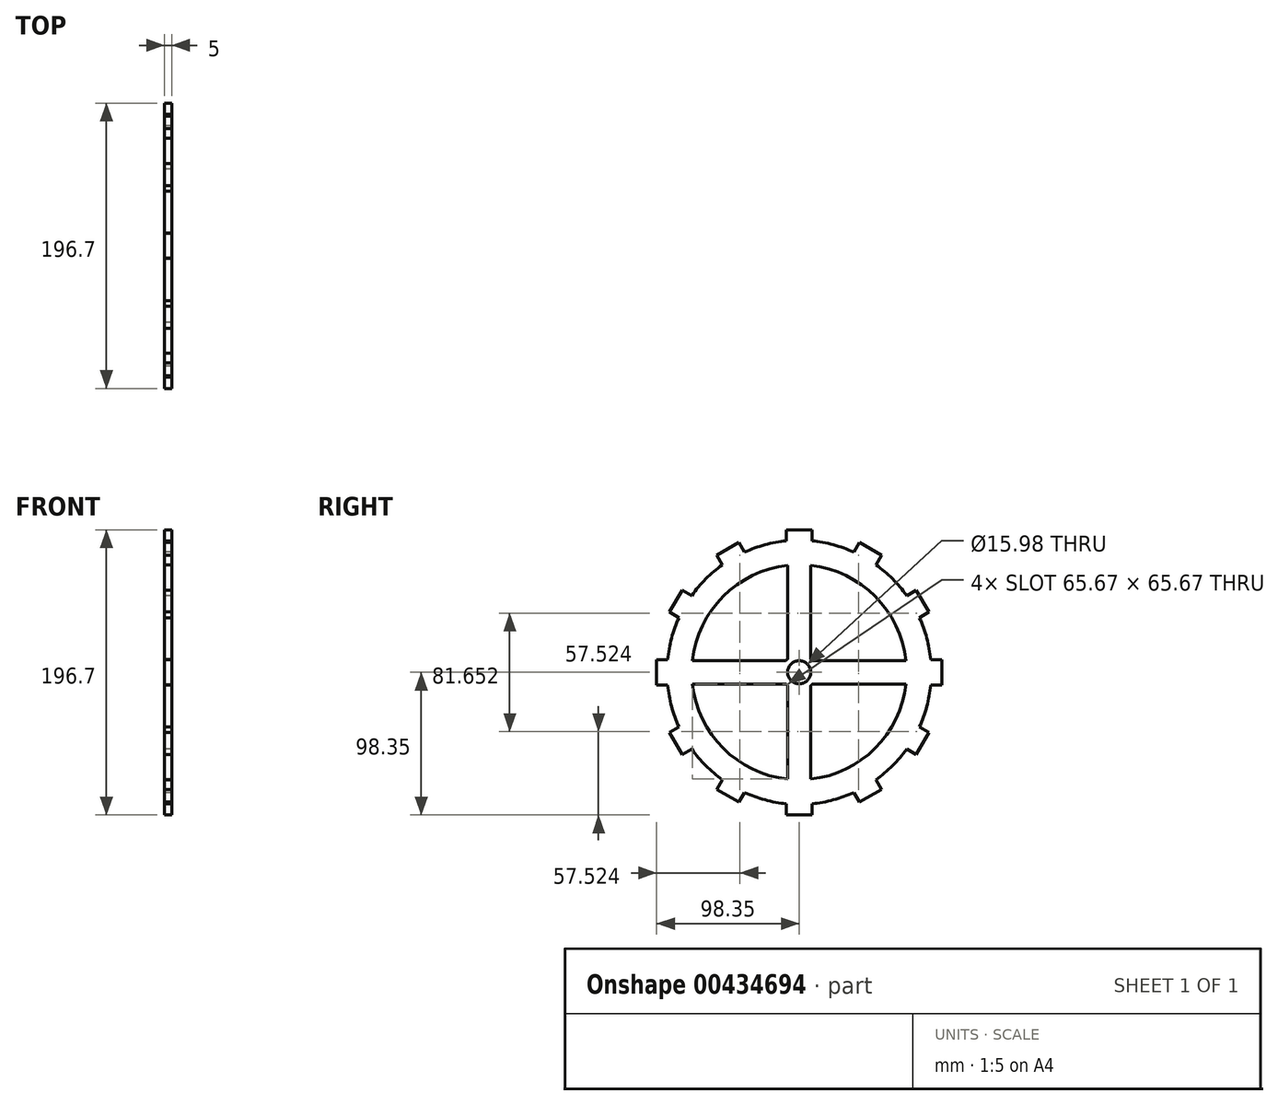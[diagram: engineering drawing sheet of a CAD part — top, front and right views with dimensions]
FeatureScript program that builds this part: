
annotation { "Feature Type Name" : "Feature", "Feature Type Description" : "" }
export const myFeature = defineFeature(function(context is Context, id is Id, definition is map)
    precondition{}
    {
        {
            var Q0;
            Q0=qCreatedBy(makeId("Right.planeOp"),FACE);
            var sketch = newSketch(context, id + "F0", { "sketchPlane" : qUnion([Q0])});
            skLineSegment(sketch, "E0", {"start": v(-91.09, 0) * mm, "end": v(91.09, 0) * mm, "construction": true});
            skLineSegment(sketch, "E1", {"start": v(0, 91.09) * mm, "end": v(0, -91.09) * mm, "construction": true});
            skCircle(sketch, "E2", {"center": v(0, 0) * mm, "radius": 8 * mm});
            skCircle(sketch, "E3", {"center": v(0, 0) * mm, "radius": 12.19 * mm});
            skCircle(sketch, "E4", {"center": v(0, 0) * mm, "radius": 74.1 * mm});
            skCircle(sketch, "E5", {"center": v(0, 0) * mm, "radius": 91.09 * mm});
            skLineSegment(sketch, "E6", {"start": v(0, 12.19) * mm, "end": v(30.8, 12.19) * mm, "construction": true});
            skLineSegment(sketch, "E7", {"start": v(0, -12.19) * mm, "end": v(30.8, -12.19) * mm, "construction": true});
            skLineSegment(sketch, "E8", {"start": v(-12.19, 0) * mm, "end": v(-12.19, 23.25) * mm, "construction": true});
            skLineSegment(sketch, "E9", {"start": v(12.19, 0) * mm, "end": v(12.19, 23.25) * mm, "construction": true});
            skLineSegment(sketch, "E10", {"start": v(-8, 0) * mm, "end": v(-8, 23.25) * mm, "construction": true});
            skLineSegment(sketch, "E11", {"start": v(8, 0) * mm, "end": v(8, 23.25) * mm, "construction": true});
            skLineSegment(sketch, "E12", {"start": v(0, 8) * mm, "end": v(30.42, 8) * mm, "construction": true});
            skLineSegment(sketch, "E13", {"start": v(0, -8) * mm, "end": v(30.42, -8) * mm, "construction": true});
            skLineSegment(sketch, "E14", {"start": v(-8, 9.2) * mm, "end": v(-30.06, 9.2) * mm, "construction": true});
            skLineSegment(sketch, "E15", {"start": v(-8, -9.2) * mm, "end": v(-30.06, -9.2) * mm, "construction": true});
            skLineSegment(sketch, "E16", {"start": v(-8, 9.2) * mm, "end": v(-8, 73.66) * mm});
            skLineSegment(sketch, "E17", {"start": v(9.2, 8) * mm, "end": v(9.2, 27.63) * mm, "construction": true});
            skLineSegment(sketch, "E18", {"start": v(9.2, 8) * mm, "end": v(73.66, 8) * mm});
            skLineSegment(sketch, "E19.MirrorCS", {"start": v(8, 9.2) * mm, "end": v(8, 73.66) * mm});
            skLineSegment(sketch, "E20.MirrorCS", {"start": v(-9.2, 8) * mm, "end": v(-73.66, 8) * mm});
            skLineSegment(sketch, "E21.MirrorCS", {"start": v(-8, -9.2) * mm, "end": v(-8, -73.66) * mm});
            skLineSegment(sketch, "E22.MirrorCS", {"start": v(8, -9.2) * mm, "end": v(8, -73.66) * mm});
            skLineSegment(sketch, "E23.MirrorCS", {"start": v(-9.2, -8) * mm, "end": v(-73.66, -8) * mm});
            skLineSegment(sketch, "E24.MirrorCS", {"start": v(9.2, -8) * mm, "end": v(73.66, -8) * mm});
            skLineSegment(sketch, "E25", {"start": v(-8.78, 90.66) * mm, "end": v(-8.78, 98.35) * mm});
            skLineSegment(sketch, "E26", {"start": v(-8.78, 98.35) * mm, "end": v(0, 98.35) * mm});
            skLineSegment(sketch, "E27.MirrorCS", {"start": v(8.78, 90.66) * mm, "end": v(8.78, 98.35) * mm});
            skLineSegment(sketch, "E28.MirrorCS", {"start": v(8.78, 98.35) * mm, "end": v(0, 98.35) * mm});
            skLineSegment(sketch, "E29.1.1", {"start": v(-52.93, 74.13) * mm, "end": v(-56.78, 80.79) * mm});
            skLineSegment(sketch, "E29.1.2", {"start": v(-56.78, 80.79) * mm, "end": v(-49.18, 85.18) * mm});
            skLineSegment(sketch, "E29.1.3", {"start": v(-41.58, 89.57) * mm, "end": v(-49.18, 85.18) * mm});
            skLineSegment(sketch, "E29.1.4", {"start": v(-37.73, 82.9) * mm, "end": v(-41.58, 89.57) * mm});
            skLineSegment(sketch, "E29.2.1", {"start": v(-82.9, 37.73) * mm, "end": v(-89.57, 41.58) * mm});
            skLineSegment(sketch, "E29.2.2", {"start": v(-89.57, 41.58) * mm, "end": v(-85.18, 49.18) * mm});
            skLineSegment(sketch, "E29.2.3", {"start": v(-80.79, 56.78) * mm, "end": v(-85.18, 49.18) * mm});
            skLineSegment(sketch, "E29.2.4", {"start": v(-74.13, 52.93) * mm, "end": v(-80.79, 56.78) * mm});
            skLineSegment(sketch, "E29.3.1", {"start": v(-90.66, -8.78) * mm, "end": v(-98.35, -8.78) * mm});
            skLineSegment(sketch, "E29.3.2", {"start": v(-98.35, -8.78) * mm, "end": v(-98.35, 0) * mm});
            skLineSegment(sketch, "E29.3.3", {"start": v(-98.35, 8.78) * mm, "end": v(-98.35, 0) * mm});
            skLineSegment(sketch, "E29.3.4", {"start": v(-90.66, 8.78) * mm, "end": v(-98.35, 8.78) * mm});
            skLineSegment(sketch, "E29.4.1", {"start": v(-74.13, -52.93) * mm, "end": v(-80.79, -56.78) * mm});
            skLineSegment(sketch, "E29.4.2", {"start": v(-80.79, -56.78) * mm, "end": v(-85.18, -49.18) * mm});
            skLineSegment(sketch, "E29.4.3", {"start": v(-89.57, -41.58) * mm, "end": v(-85.18, -49.18) * mm});
            skLineSegment(sketch, "E29.4.4", {"start": v(-82.9, -37.73) * mm, "end": v(-89.57, -41.58) * mm});
            skLineSegment(sketch, "E29.5.1", {"start": v(-37.73, -82.9) * mm, "end": v(-41.58, -89.57) * mm});
            skLineSegment(sketch, "E29.5.2", {"start": v(-41.58, -89.57) * mm, "end": v(-49.18, -85.18) * mm});
            skLineSegment(sketch, "E29.5.3", {"start": v(-56.78, -80.79) * mm, "end": v(-49.18, -85.18) * mm});
            skLineSegment(sketch, "E29.5.4", {"start": v(-52.93, -74.13) * mm, "end": v(-56.78, -80.79) * mm});
            skLineSegment(sketch, "E29.6.1", {"start": v(8.78, -90.66) * mm, "end": v(8.78, -98.35) * mm});
            skLineSegment(sketch, "E29.6.2", {"start": v(8.78, -98.35) * mm, "end": v(0, -98.35) * mm});
            skLineSegment(sketch, "E29.6.3", {"start": v(-8.78, -98.35) * mm, "end": v(0, -98.35) * mm});
            skLineSegment(sketch, "E29.6.4", {"start": v(-8.78, -90.66) * mm, "end": v(-8.78, -98.35) * mm});
            skLineSegment(sketch, "E29.7.1", {"start": v(52.93, -74.13) * mm, "end": v(56.78, -80.79) * mm});
            skLineSegment(sketch, "E29.7.2", {"start": v(56.78, -80.79) * mm, "end": v(49.18, -85.18) * mm});
            skLineSegment(sketch, "E29.7.3", {"start": v(41.58, -89.57) * mm, "end": v(49.18, -85.18) * mm});
            skLineSegment(sketch, "E29.7.4", {"start": v(37.73, -82.9) * mm, "end": v(41.58, -89.57) * mm});
            skLineSegment(sketch, "E29.8.1", {"start": v(82.9, -37.73) * mm, "end": v(89.57, -41.58) * mm});
            skLineSegment(sketch, "E29.8.2", {"start": v(89.57, -41.58) * mm, "end": v(85.18, -49.18) * mm});
            skLineSegment(sketch, "E29.8.3", {"start": v(80.79, -56.78) * mm, "end": v(85.18, -49.18) * mm});
            skLineSegment(sketch, "E29.8.4", {"start": v(74.13, -52.93) * mm, "end": v(80.79, -56.78) * mm});
            skLineSegment(sketch, "E29.9.1", {"start": v(90.66, 8.78) * mm, "end": v(98.35, 8.78) * mm});
            skLineSegment(sketch, "E29.9.2", {"start": v(98.35, 8.78) * mm, "end": v(98.35, 0) * mm});
            skLineSegment(sketch, "E29.9.3", {"start": v(98.35, -8.78) * mm, "end": v(98.35, 0) * mm});
            skLineSegment(sketch, "E29.9.4", {"start": v(90.66, -8.78) * mm, "end": v(98.35, -8.78) * mm});
            skLineSegment(sketch, "E29.10.1", {"start": v(74.13, 52.93) * mm, "end": v(80.79, 56.78) * mm});
            skLineSegment(sketch, "E29.10.2", {"start": v(80.79, 56.78) * mm, "end": v(85.18, 49.18) * mm});
            skLineSegment(sketch, "E29.10.3", {"start": v(89.57, 41.58) * mm, "end": v(85.18, 49.18) * mm});
            skLineSegment(sketch, "E29.10.4", {"start": v(82.9, 37.73) * mm, "end": v(89.57, 41.58) * mm});
            skLineSegment(sketch, "E29.11.1", {"start": v(37.73, 82.9) * mm, "end": v(41.58, 89.57) * mm});
            skLineSegment(sketch, "E29.11.2", {"start": v(41.58, 89.57) * mm, "end": v(49.18, 85.18) * mm});
            skLineSegment(sketch, "E29.11.3", {"start": v(56.78, 80.79) * mm, "end": v(49.18, 85.18) * mm});
            skLineSegment(sketch, "E29.11.4", {"start": v(52.93, 74.13) * mm, "end": v(56.78, 80.79) * mm});
            skSolve(sketch);
        }
        {
            var Q0;
            Q0=makeQuery(id+"F0.imprint","IMPRINT",FACE,{"disambiguationData":[TD([[makeQuery(id+"F0.imprint","IMPRINT",EDGE,{"derivedFrom":sQuery(id+"F0.wireOp",EDGE,"E5")}),1.0]])]});
            var Q1;
            {var subQ0=sQuery(id+"F0.wireOp",EDGE,"E16");Q1=makeQuery(id+"F0.imprint","IMPRINT",FACE,{"disambiguationData":[TD([[makeQuery(id+"F0.imprint","IMPRINT",EDGE,{"derivedFrom":subQ0}),-1.0]])]});}
            var Q2;
            Q2=makeQuery(id+"F0.imprint","IMPRINT",FACE,{"disambiguationData":[TD([[makeQuery(id+"F0.imprint","IMPRINT",EDGE,{"derivedFrom":sQuery(id+"F0.wireOp",EDGE,"E2")}),-1.0]])]});
            var Q3;
            {var subQ0=sQuery(id+"F0.wireOp",EDGE,"E20.MirrorCS");Q3=makeQuery(id+"F0.imprint","IMPRINT",FACE,{"disambiguationData":[TD([[makeQuery(id+"F0.imprint","IMPRINT",EDGE,{"derivedFrom":subQ0}),1.0]])]});}
            var Q4;
            {var subQ0=sQuery(id+"F0.wireOp",EDGE,"E18");Q4=makeQuery(id+"F0.imprint","IMPRINT",FACE,{"disambiguationData":[TD([[makeQuery(id+"F0.imprint","IMPRINT",EDGE,{"derivedFrom":subQ0}),-1.0]])]});}
            var Q5;
            {var subQ0=sQuery(id+"F0.wireOp",EDGE,"E21.MirrorCS");Q5=makeQuery(id+"F0.imprint","IMPRINT",FACE,{"disambiguationData":[TD([[makeQuery(id+"F0.imprint","IMPRINT",EDGE,{"derivedFrom":subQ0}),1.0]])]});}
            var Q6;
            {var subQ11=sQuery(id+"F0.wireOp",EDGE,"E4");var subQ18=makeQuery(id+"F0.imprint","INTERSECT",VERTEX,{"derivedFrom":[subQ11,sQuery(id+"F0.wireOp",EDGE,"E18")]});Q6=makeQuery(id+"F0.imprint","IMPRINT",FACE,{"disambiguationData":[TD([[makeQuery(id+"F0.imprint","IMPRINT",EDGE,{"disambiguationData":[TD([[subQ18,-1.0]])],"derivedFrom":subQ11}),-1.0]])]});}
            var Q7;
            {var subQ1=sQuery(id+"F0.wireOp",EDGE,"E25");Q7=makeQuery(id+"F0.imprint","IMPRINT",FACE,{"disambiguationData":[TD([[makeQuery(id+"F0.imprint","IMPRINT",EDGE,{"derivedFrom":subQ1}),-1.0]])]});}
            var Q8;
            {var subQ0=sQuery(id+"F0.wireOp",EDGE,"E29.11.1");Q8=makeQuery(id+"F0.imprint","IMPRINT",FACE,{"disambiguationData":[TD([[makeQuery(id+"F0.imprint","IMPRINT",EDGE,{"derivedFrom":subQ0}),-1.0]])]});}
            var Q9;
            {var subQ1=sQuery(id+"F0.wireOp",EDGE,"E29.10.1");Q9=makeQuery(id+"F0.imprint","IMPRINT",FACE,{"disambiguationData":[TD([[makeQuery(id+"F0.imprint","IMPRINT",EDGE,{"derivedFrom":subQ1}),-1.0]])]});}
            var Q10;
            {var subQ1=sQuery(id+"F0.wireOp",EDGE,"E29.9.1");Q10=makeQuery(id+"F0.imprint","IMPRINT",FACE,{"disambiguationData":[TD([[makeQuery(id+"F0.imprint","IMPRINT",EDGE,{"derivedFrom":subQ1}),-1.0]])]});}
            var Q11;
            {var subQ2=sQuery(id+"F0.wireOp",EDGE,"E29.8.1");Q11=makeQuery(id+"F0.imprint","IMPRINT",FACE,{"disambiguationData":[TD([[makeQuery(id+"F0.imprint","IMPRINT",EDGE,{"derivedFrom":subQ2}),-1.0]])]});}
            var Q12;
            {var subQ1=sQuery(id+"F0.wireOp",EDGE,"E29.7.1");Q12=makeQuery(id+"F0.imprint","IMPRINT",FACE,{"disambiguationData":[TD([[makeQuery(id+"F0.imprint","IMPRINT",EDGE,{"derivedFrom":subQ1}),-1.0]])]});}
            var Q13;
            {var subQ1=sQuery(id+"F0.wireOp",EDGE,"E29.6.1");Q13=makeQuery(id+"F0.imprint","IMPRINT",FACE,{"disambiguationData":[TD([[makeQuery(id+"F0.imprint","IMPRINT",EDGE,{"derivedFrom":subQ1}),-1.0]])]});}
            var Q14;
            {var subQ1=sQuery(id+"F0.wireOp",EDGE,"E29.5.1");Q14=makeQuery(id+"F0.imprint","IMPRINT",FACE,{"disambiguationData":[TD([[makeQuery(id+"F0.imprint","IMPRINT",EDGE,{"derivedFrom":subQ1}),-1.0]])]});}
            var Q15;
            {var subQ1=sQuery(id+"F0.wireOp",EDGE,"E29.4.1");Q15=makeQuery(id+"F0.imprint","IMPRINT",FACE,{"disambiguationData":[TD([[makeQuery(id+"F0.imprint","IMPRINT",EDGE,{"derivedFrom":subQ1}),-1.0]])]});}
            var Q16;
            {var subQ2=sQuery(id+"F0.wireOp",EDGE,"E29.3.1");Q16=makeQuery(id+"F0.imprint","IMPRINT",FACE,{"disambiguationData":[TD([[makeQuery(id+"F0.imprint","IMPRINT",EDGE,{"derivedFrom":subQ2}),-1.0]])]});}
            var Q17;
            {var subQ2=sQuery(id+"F0.wireOp",EDGE,"E29.2.1");Q17=makeQuery(id+"F0.imprint","IMPRINT",FACE,{"disambiguationData":[TD([[makeQuery(id+"F0.imprint","IMPRINT",EDGE,{"derivedFrom":subQ2}),-1.0]])]});}
            var Q18;
            {var subQ1=sQuery(id+"F0.wireOp",EDGE,"E29.1.1");Q18=makeQuery(id+"F0.imprint","IMPRINT",FACE,{"disambiguationData":[TD([[makeQuery(id+"F0.imprint","IMPRINT",EDGE,{"derivedFrom":subQ1}),-1.0]])]});}
            extrude(context, id + "F1", {"entities" : qUnion([Q0, Q1, Q2, Q3, Q4, Q5, Q6, Q7, Q8, Q9, Q10, Q11, Q12, Q13, Q14, Q15, Q16, Q17, Q18]), "depth" : 5 * mm, "symmetric" : true});
        }
    });
